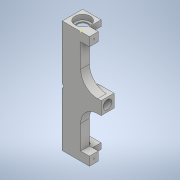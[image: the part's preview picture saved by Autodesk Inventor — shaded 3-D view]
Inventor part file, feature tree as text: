
AUTODESK INVENTOR PART (.ipt)
format: ipt  version: 2020 (Build 240168000, 168)  size: 647,680 bytes
history: native  units: mm
features: extrude x25, sketch x25, fillet x5
ambient origin geometry x8: Origin, YZ Plane, XZ Plane, XY Plane, X Axis, Y Axis, Z Axis, Center Point
bodies: Solid1 (feature_tree)
feature tree (55):
  extrude  "Extrusion1"  Depth=165.0mm
  extrude  "Extrusion2"  Depth=8.5mm
  extrude  "Extrusion3"  Depth=25.0mm TaperAngle=0.0deg
  extrude  "Extrusion4"  Depth=25.0mm
  extrude  "Extrusion5"  Depth=7.1mm
  extrude  "Extrusion6"  Depth=7.1mm TaperAngle=0.0deg
  fillet  "Fillet1"  Radius=5.0mm
  extrude  "Extrusion7"  Depth=10.0mm TaperAngle=0.0deg
  fillet  "Fillet2"  Radius=2.0mm
  extrude  "Extrusion8"  Depth=8.0mm
  extrude  "Extrusion9"  Depth=8.0mm
  fillet  "Fillet3"  Radius=8.0mm
  extrude  "Extrusion10"  Depth=6.0mm
  extrude  "Extrusion11"  Depth=3.5mm
  fillet  "Fillet4"  Radius=12.25mm
  extrude  "Extrusion12"  Depth=12.25mm
  extrude  "Extrusion13"  Depth=3.5mm
  extrude  "Extrusion14"  Depth=1.0mm
  sketch  "Sketch16"  dims[d40=2.0mm d41=8.0mm]
  extrude  "Extrusion15"  Depth=8.0mm
  extrude  "Extrusion16"  Depth=2.0mm
  extrude  "Extrusion17"  Depth=6.0mm
  extrude  "Extrusion18"  Depth=4.0mm
  extrude  "Extrusion19"  Depth=6.5mm TaperAngle=0.0deg
  extrude  "Extrusion20"  Depth=8.0mm TaperAngle=0.0deg
  extrude  "Extrusion21"  Depth=1.0mm
  fillet  "Fillet5"  Radius=1.0mm
  extrude  "Extrusion22"  Depth=7.1mm TaperAngle=0.0deg
  extrude  "Extrusion23"  Depth=2.0mm TaperAngle=0.0deg
  extrude  "Extrusion24"  Depth=2.0mm TaperAngle=0.0deg
  extrude  "Extrusion25"  Depth=165.0mm TaperAngle=0.0deg
  sketch  "Sketch1"  dims[d0=25.0mm d1=165.0mm]
  sketch  "Sketch2"  dims[d2=3.0mm d3=0.0mm d4=8.5mm]
  sketch  "Sketch3"  dims[d5=8.5mm d6=25.0mm d7=0.0mm]
  sketch  "Sketch4"  dims[d8=25.0mm d9=22.75mm]
  sketch  "Sketch5"  dims[d10=7.1mm d11=0.0mm d12=15.5mm]
  sketch  "Sketch6"  dims[d13=165.0mm d14=0.0mm d15=7.1mm d16=0.0mm d17=5.0mm]
  sketch  "Sketch7"  dims[d18=5.0mm d19=10.0mm d20=0.0mm d21=2.0mm]
  sketch  "Sketch8"  dims[d22=16.0mm d23=8.0mm]
  sketch  "Sketch9"  dims[d24=16.0mm d25=16.0mm d26=8.0mm]
  sketch  "Sketch10"  dims[d27=45.0mm d28=0.0mm d29=6.0mm]
  sketch  "Sketch11"  dims[d30=12.25mm d31=3.5mm d32=12.25mm]
  sketch  "Sketch13"  dims[d33=3.5mm d34=12.25mm]
  sketch  "Sketch14"  dims[d35=12.25mm d36=3.5mm]
  sketch  "Sketch15"  dims[d37=40.0mm d38=0.0mm d39=1.0mm]
  sketch  "Sketch17"  dims[d42=1.0mm d43=2.0mm]
  sketch  "Sketch18"  dims[d44=12.0mm d45=0.0mm d46=6.0mm]
  sketch  "Sketch19"  dims[d47=6.0mm d48=4.0mm]
  sketch  "Sketch20"  dims[d49=8.0mm d50=6.5mm d51=0.0mm]
  sketch  "Sketch21"  dims[d52=6.35mm d53=8.0mm d54=0.0mm]
  sketch  "Sketch22"  dims[d55=6.5mm d56=47.0mm d57=1.0mm]
  sketch  "Sketch23"  dims[d58=7.0mm d59=0.0mm d60=7.1mm d61=0.0mm]
  sketch  "Sketch24"  dims[d62=14.5mm d63=0.0mm d64=2.0mm d65=0.0mm]
  sketch  "Sketch25"  dims[d66=8.5mm d67=2.0mm d68=0.0mm]
  sketch  "Sketch26"  dims[d69=20.0mm d70=0.0mm d71=165.0mm d72=0.0mm d73=47.0mm d74=0.0mm d75=6.0mm d76=148.0mm d77=0.0mm d78=60.0mm d79=19.05mm d80=19.05mm d81=0.0mm d82=25.0mm d83=6.0mm d84=26.8mm d85=0.0mm d86=12.954mm d87=20.0mm d88=0.0mm d89=12.917mm d90=12.917mm d91=12.917mm d92=0.0mm d93=2.0mm d94=2.0mm d95=5.0mm d96=0.0mm]
